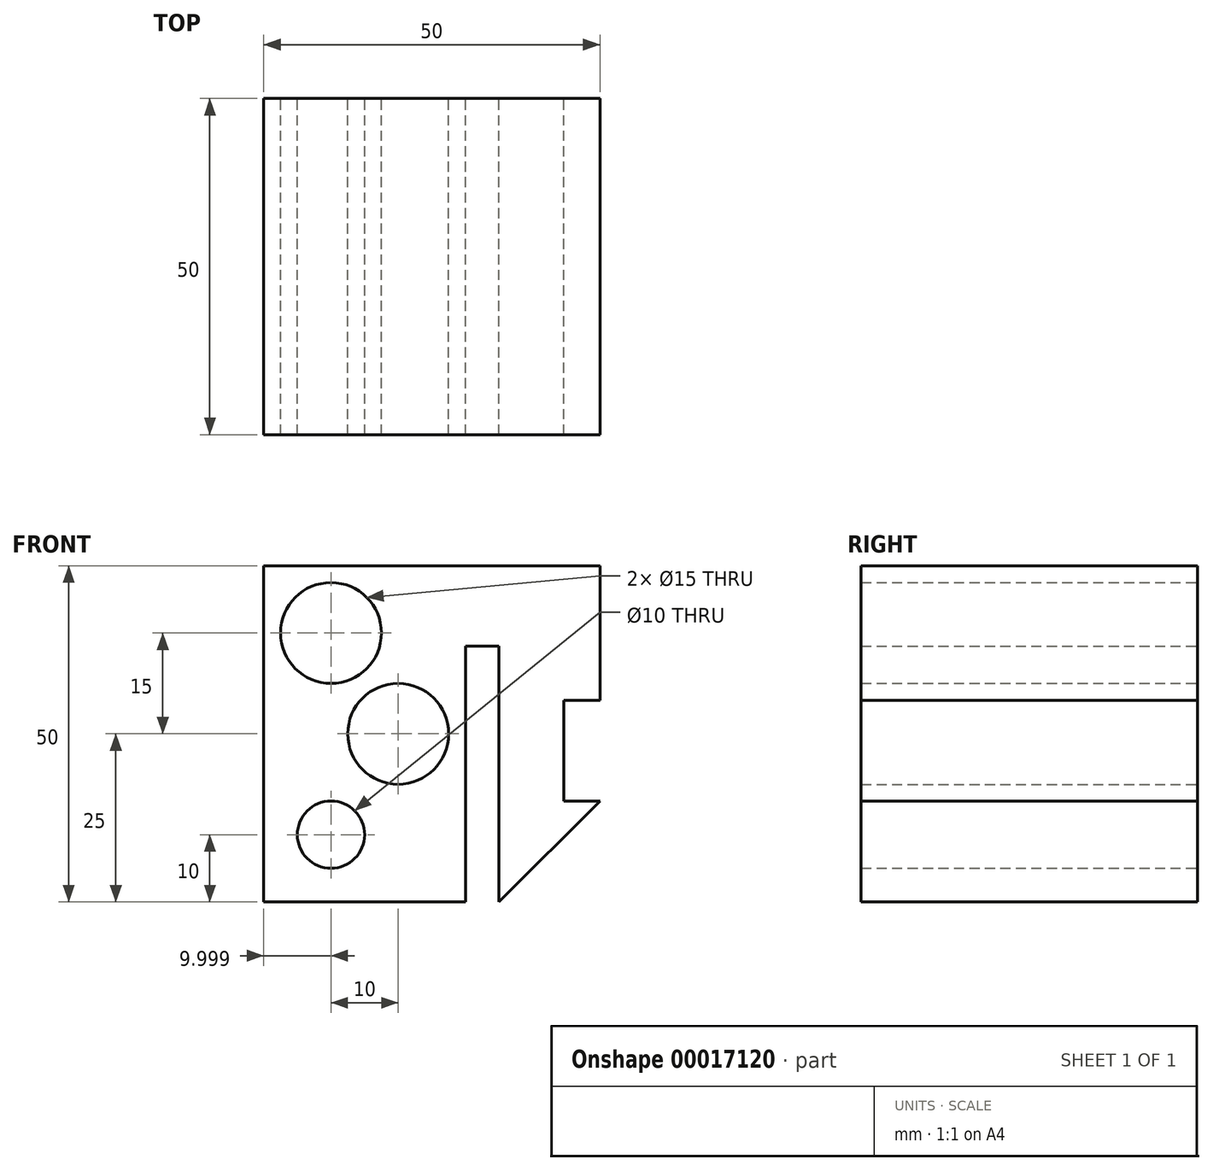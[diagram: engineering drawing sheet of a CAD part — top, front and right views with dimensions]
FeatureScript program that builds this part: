
annotation { "Feature Type Name" : "Feature", "Feature Type Description" : "" }
export const myFeature = defineFeature(function(context is Context, id is Id, definition is map)
    precondition{}
    {
        {
            var Q0;
            Q0=qCreatedBy(makeId("Front.planeOp"),FACE);
            var sketch = newSketch(context, id + "F0", { "sketchPlane" : qUnion([Q0])});
            skLineSegment(sketch, "E0", {"start": v(-30.63, 34.45) * mm, "end": v(-30.63, -15.55) * mm});
            skLineSegment(sketch, "E1", {"start": v(-30.63, -15.55) * mm, "end": v(-0.63, -15.55) * mm});
            skLineSegment(sketch, "E2", {"start": v(-0.63, -15.55) * mm, "end": v(-0.63, 22.5) * mm});
            skLineSegment(sketch, "E3", {"start": v(-0.63, 22.5) * mm, "end": v(4.37, 22.5) * mm});
            skLineSegment(sketch, "E4", {"start": v(4.37, 22.5) * mm, "end": v(4.37, -15.55) * mm});
            skLineSegment(sketch, "E5", {"start": v(4.37, -15.55) * mm, "end": v(19.37, -0.55) * mm});
            skLineSegment(sketch, "E6", {"start": v(19.37, -0.55) * mm, "end": v(14, -0.55) * mm});
            skLineSegment(sketch, "E7", {"start": v(14, -0.55) * mm, "end": v(14, 14.45) * mm});
            skLineSegment(sketch, "E8", {"start": v(14, 14.45) * mm, "end": v(19.37, 14.45) * mm});
            skLineSegment(sketch, "E9", {"start": v(19.37, 14.45) * mm, "end": v(19.37, 34.45) * mm});
            skLineSegment(sketch, "E10", {"start": v(19.37, 34.45) * mm, "end": v(-30.63, 34.45) * mm});
            skCircle(sketch, "E11", {"center": v(-20.63, 24.45) * mm, "radius": 7.5 * mm});
            skCircle(sketch, "E12", {"center": v(-20.63, -5.55) * mm, "radius": 5 * mm});
            skCircle(sketch, "E13", {"center": v(-10.63, 9.45) * mm, "radius": 7.5 * mm});
            skSolve(sketch);
        }
        {
            var Q0;
            Q0 = qSketchRegion(id + "F0", true);
            extrude(context, id + "F1", {"entities" : qUnion([Q0]), "depth" : 50 * mm});
        }
    });
